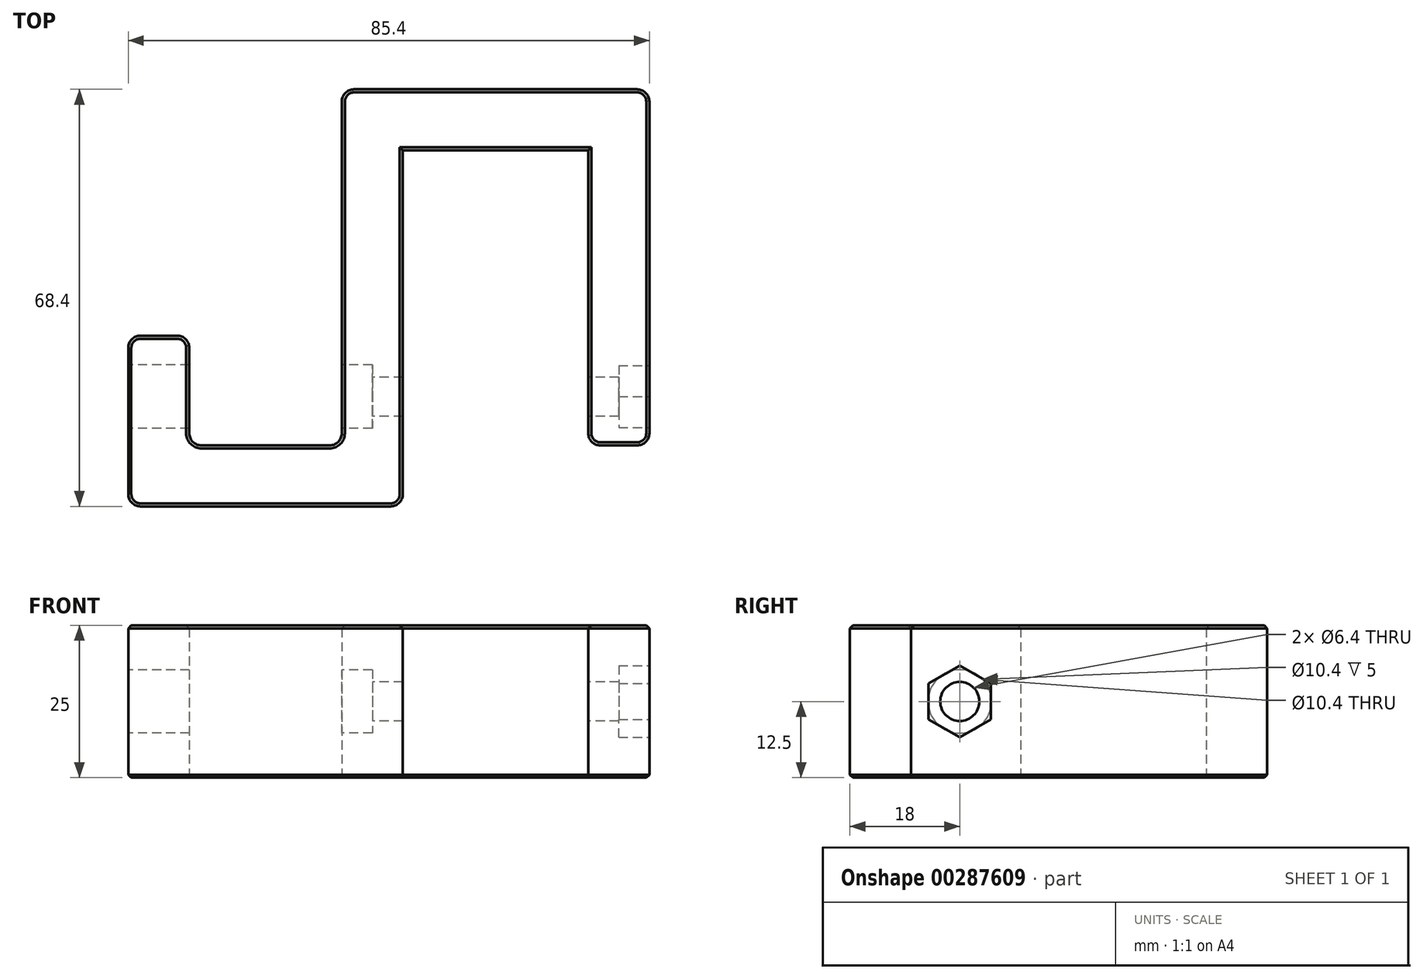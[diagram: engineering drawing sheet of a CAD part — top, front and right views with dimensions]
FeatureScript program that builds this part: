
annotation { "Feature Type Name" : "Feature", "Feature Type Description" : "" }
export const myFeature = defineFeature(function(context is Context, id is Id, definition is map)
    precondition{}
    {
        {
            var Q0;
            Q0=qCreatedBy(makeId("Top.planeOp"),FACE);
            var sketch = newSketch(context, id + "F0", { "sketchPlane" : qUnion([Q0])});
            skLineSegment(sketch, "E0.bottom", {"start": v(15.2, -15.2) * mm, "end": v(-15.2, -15.2) * mm, "construction": true});
            skLineSegment(sketch, "E0.top", {"start": v(15.2, 15.2) * mm, "end": v(-15.2, 15.2) * mm, "construction": true});
            skLineSegment(sketch, "E0.left", {"start": v(15.2, -15.2) * mm, "end": v(15.2, 15.2) * mm, "construction": true});
            skLineSegment(sketch, "E0.right", {"start": v(-15.2, -15.2) * mm, "end": v(-15.2, 15.2) * mm, "construction": true});
            skPoint(sketch, "E0.middle", {"position": v(0, 0) * mm});
            skLineSegment(sketch, "E1", {"start": v(15.2, 15.2) * mm, "end": v(15.2, -33.2) * mm});
            skLineSegment(sketch, "E2", {"start": v(15.2, -33.2) * mm, "end": v(25.2, -33.2) * mm});
            skLineSegment(sketch, "E3", {"start": v(25.2, -33.2) * mm, "end": v(25.2, 25.2) * mm});
            skLineSegment(sketch, "E4", {"start": v(25.2, 25.2) * mm, "end": v(-25.2, 25.2) * mm});
            skLineSegment(sketch, "E5", {"start": v(-25.2, 25.2) * mm, "end": v(-25.2, -33.2) * mm});
            skLineSegment(sketch, "E6", {"start": v(-25.2, -33.2) * mm, "end": v(-15.2, -33.2) * mm});
            skLineSegment(sketch, "E7", {"start": v(-15.2, -33.2) * mm, "end": v(-15.2, 15.2) * mm});
            skLineSegment(sketch, "E8.bottom", {"start": v(-15.2, -33.2) * mm, "end": v(-60.2, -33.2) * mm});
            skLineSegment(sketch, "E8.top", {"start": v(-15.2, -43.2) * mm, "end": v(-60.2, -43.2) * mm});
            skLineSegment(sketch, "E8.left", {"start": v(-15.2, -33.2) * mm, "end": v(-15.2, -43.2) * mm});
            skLineSegment(sketch, "E8.right", {"start": v(-60.2, -33.2) * mm, "end": v(-60.2, -43.2) * mm});
            skLineSegment(sketch, "E9.bottom", {"start": v(-60.2, -33.2) * mm, "end": v(-50.2, -33.2) * mm});
            skLineSegment(sketch, "E9.top", {"start": v(-60.2, -15.2) * mm, "end": v(-50.2, -15.2) * mm});
            skLineSegment(sketch, "E9.left", {"start": v(-60.2, -33.2) * mm, "end": v(-60.2, -15.2) * mm});
            skLineSegment(sketch, "E9.right", {"start": v(-50.2, -33.2) * mm, "end": v(-50.2, -15.2) * mm});
            skLineSegment(sketch, "E10", {"start": v(-15.2, 15.2) * mm, "end": v(15.2, 15.2) * mm});
            skSolve(sketch);
        }
        {
            var Q0;
            Q0 = qSketchRegion(id + "F0", true);
            extrude(context, id + "F1", {"entities" : qUnion([Q0]), "depth" : 25 * mm, "offsetDistance" : 25 * mm});
        }
        {
            var Q0;
            Q0=makeQuery(id+"F1.opExtrude","SWEPT_FACE",FACE,{"disambiguationData":[OSD([sQuery(id+"F0.wireOp",EDGE,"E5")])]});
            var sketch = newSketch(context, id + "F2", { "sketchPlane" : qUnion([Q0])});
            skPoint(sketch, "E11", {"position": v(33.2, 12.5) * mm});
            skCircle(sketch, "E12", {"center": v(25.2, 12.5) * mm, "radius": 3.2 * mm});
            skCircle(sketch, "E13", {"center": v(25.2, 12.5) * mm, "radius": 5.2 * mm});
            skSolve(sketch);
        }
        {
            var Q0;
            Q0=makeQuery(id+"F2.imprint","IMPRINT",FACE,{"disambiguationData":[TD([[makeQuery(id+"F2.imprint","IMPRINT",EDGE,{"derivedFrom":sQuery(id+"F2.wireOp",EDGE,"E12")}),1.0]])]});
            extrude(context, id + "F3", {"entities" : qUnion([Q0]), "operationType" : NewBodyOperationType.REMOVE, "endBound" : BoundingType.THROUGH_ALL, "oppositeDirection" : true, "depth" : 25 * mm, "offsetDistance" : 25 * mm, "hasSecondDirection" : true, "secondDirectionBound" : BoundingType.THROUGH_ALL, "secondDirectionOppositeDirection" : false, "secondDirectionDepth" : 25 * mm});
        }
        {
            var Q0;
            Q0=makeQuery(id+"F2.imprint","IMPRINT",FACE,{"disambiguationData":[TD([[makeQuery(id+"F2.imprint","IMPRINT",EDGE,{"derivedFrom":sQuery(id+"F2.wireOp",EDGE,"E12")}),-1.0]])]});
            extrude(context, id + "F4", {"entities" : qUnion([Q0]), "operationType" : NewBodyOperationType.REMOVE, "oppositeDirection" : true, "depth" : 5 * mm, "offsetDistance" : 25 * mm, "hasSecondDirection" : true, "secondDirectionBound" : BoundingType.THROUGH_ALL, "secondDirectionOppositeDirection" : false, "secondDirectionDepth" : 25 * mm});
        }
        {
            var Q0;
            Q0=makeQuery(id+"F1.opExtrude","SWEPT_FACE",FACE,{"disambiguationData":[OSD([sQuery(id+"F0.wireOp",EDGE,"E3")])]});
            var sketch = newSketch(context, id + "F5", { "sketchPlane" : qUnion([Q0])});
            skCircle(sketch, "E14.cCircle", {"center": v(-25.2, 12.5) * mm, "radius": 5.1 * mm, "construction": true});
            skLineSegment(sketch, "E14.0", {"start": v(-25.2, 6.61) * mm, "end": v(-30.3, 9.56) * mm});
            skLineSegment(sketch, "E14.1", {"start": v(-30.3, 9.56) * mm, "end": v(-30.3, 15.44) * mm});
            skLineSegment(sketch, "E14.2", {"start": v(-30.3, 15.44) * mm, "end": v(-25.2, 18.39) * mm});
            skLineSegment(sketch, "E14.3", {"start": v(-25.2, 18.39) * mm, "end": v(-20.1, 15.44) * mm});
            skLineSegment(sketch, "E14.4", {"start": v(-20.1, 15.44) * mm, "end": v(-20.1, 9.56) * mm});
            skLineSegment(sketch, "E14.5", {"start": v(-20.1, 9.56) * mm, "end": v(-25.2, 6.61) * mm});
            skPoint(sketch, "E14.0.midPoint", {"position": v(-27.75, 8.08) * mm});
            skSolve(sketch);
        }
        {
            var Q0;
            Q0=makeQuery(id+"F5.imprint","IMPRINT",FACE,{"disambiguationData":[TD([[makeQuery(id+"F5.imprint","IMPRINT",EDGE,{"derivedFrom":sQuery(id+"F5.wireOp",EDGE,"E14.0")}),-1.0]])]});
            extrude(context, id + "F6", {"entities" : qUnion([Q0]), "operationType" : NewBodyOperationType.REMOVE, "oppositeDirection" : true, "depth" : 5 * mm, "offsetDistance" : 25 * mm});
        }
        {
            var Q0;
            Q0=makeQuery(id+"F1.opExtrude","SWEPT_EDGE",EDGE,{"disambiguationData":[OSD([sQuery(id+"F0.wireOp",EDGE,"E5"),sQuery(id+"F0.wireOp",EDGE,"E8.bottom")])]});
            var Q1;
            Q1=makeQuery(id+"F1.opExtrude","SWEPT_EDGE",EDGE,{"disambiguationData":[OSD([sQuery(id+"F0.wireOp",EDGE,"E8.top"),sQuery(id+"F0.wireOp",EDGE,"E8.left")])]});
            var Q2;
            Q2=makeQuery(id+"F1.opExtrude","SWEPT_EDGE",EDGE,{"disambiguationData":[OSD([sQuery(id+"F0.wireOp",EDGE,"E2"),sQuery(id+"F0.wireOp",EDGE,"E1")])]});
            var Q3;
            Q3=makeQuery(id+"F1.opExtrude","SWEPT_EDGE",EDGE,{"disambiguationData":[OSD([sQuery(id+"F0.wireOp",EDGE,"E2"),sQuery(id+"F0.wireOp",EDGE,"E3")])]});
            var Q4;
            Q4=makeQuery(id+"F1.opExtrude","SWEPT_EDGE",EDGE,{"disambiguationData":[OSD([sQuery(id+"F0.wireOp",EDGE,"E3"),sQuery(id+"F0.wireOp",EDGE,"E4")])]});
            var Q5;
            Q5=makeQuery(id+"F1.opExtrude","SWEPT_EDGE",EDGE,{"disambiguationData":[OSD([sQuery(id+"F0.wireOp",EDGE,"E8.bottom"),sQuery(id+"F0.wireOp",EDGE,"E9.bottom"),sQuery(id+"F0.wireOp",EDGE,"E9.right")])]});
            var Q6;
            Q6=makeQuery(id+"F1.opExtrude","SWEPT_EDGE",EDGE,{"disambiguationData":[OSD([sQuery(id+"F0.wireOp",EDGE,"E9.top"),sQuery(id+"F0.wireOp",EDGE,"E9.right")])]});
            var Q7;
            Q7=makeQuery(id+"F1.opExtrude","SWEPT_EDGE",EDGE,{"disambiguationData":[OSD([sQuery(id+"F0.wireOp",EDGE,"E9.top"),sQuery(id+"F0.wireOp",EDGE,"E9.left")])]});
            var Q8;
            Q8=makeQuery(id+"F1.opExtrude","SWEPT_EDGE",EDGE,{"disambiguationData":[OSD([sQuery(id+"F0.wireOp",EDGE,"E8.top"),sQuery(id+"F0.wireOp",EDGE,"E8.right")])]});
            var Q9;
            Q9=makeQuery(id+"F1.opExtrude","SWEPT_EDGE",EDGE,{"disambiguationData":[OSD([sQuery(id+"F0.wireOp",EDGE,"E4"),sQuery(id+"F0.wireOp",EDGE,"E5")])]});
            fillet(context, id + "F7", {"entities" : qUnion([Q0, Q1, Q2, Q3, Q4, Q5, Q6, Q7, Q8, Q9]), "tangentPropagation" : true, "radius" : 2 * mm, "defaultsChanged" : false, "vertexSettings" : [], "allowEdgeOverflow" : false});
        }
        {
            var Q0;
            Q0=makeQuery(id+"F1.opExtrude","CAP_FACE",FACE,{"disambiguationData":[OSD([sQuery(id+"F0.wireOp",EDGE,"E2"),sQuery(id+"F0.wireOp",EDGE,"E3"),sQuery(id+"F0.wireOp",EDGE,"E4"),sQuery(id+"F0.wireOp",EDGE,"E5"),sQuery(id+"F0.wireOp",EDGE,"E7"),sQuery(id+"F0.wireOp",EDGE,"E1"),sQuery(id+"F0.wireOp",EDGE,"E8.bottom"),sQuery(id+"F0.wireOp",EDGE,"E8.top"),sQuery(id+"F0.wireOp",EDGE,"E8.left"),sQuery(id+"F0.wireOp",EDGE,"E8.right"),sQuery(id+"F0.wireOp",EDGE,"E9.top"),sQuery(id+"F0.wireOp",EDGE,"E9.left"),sQuery(id+"F0.wireOp",EDGE,"E9.right"),sQuery(id+"F0.wireOp",EDGE,"E10")])],"isStart":false});
            var Q1;
            Q1=makeQuery(id+"F1.opExtrude","CAP_FACE",FACE,{"disambiguationData":[OSD([sQuery(id+"F0.wireOp",EDGE,"E2"),sQuery(id+"F0.wireOp",EDGE,"E3"),sQuery(id+"F0.wireOp",EDGE,"E4"),sQuery(id+"F0.wireOp",EDGE,"E5"),sQuery(id+"F0.wireOp",EDGE,"E7"),sQuery(id+"F0.wireOp",EDGE,"E1"),sQuery(id+"F0.wireOp",EDGE,"E8.bottom"),sQuery(id+"F0.wireOp",EDGE,"E8.top"),sQuery(id+"F0.wireOp",EDGE,"E8.left"),sQuery(id+"F0.wireOp",EDGE,"E8.right"),sQuery(id+"F0.wireOp",EDGE,"E9.top"),sQuery(id+"F0.wireOp",EDGE,"E9.left"),sQuery(id+"F0.wireOp",EDGE,"E9.right"),sQuery(id+"F0.wireOp",EDGE,"E10")])],"isStart":true});
            chamfer(context, id + "F8", {"entities" : qUnion([Q0, Q1]), "width" : 0.5 * mm, "tangentPropagation" : true});
        }
    });
